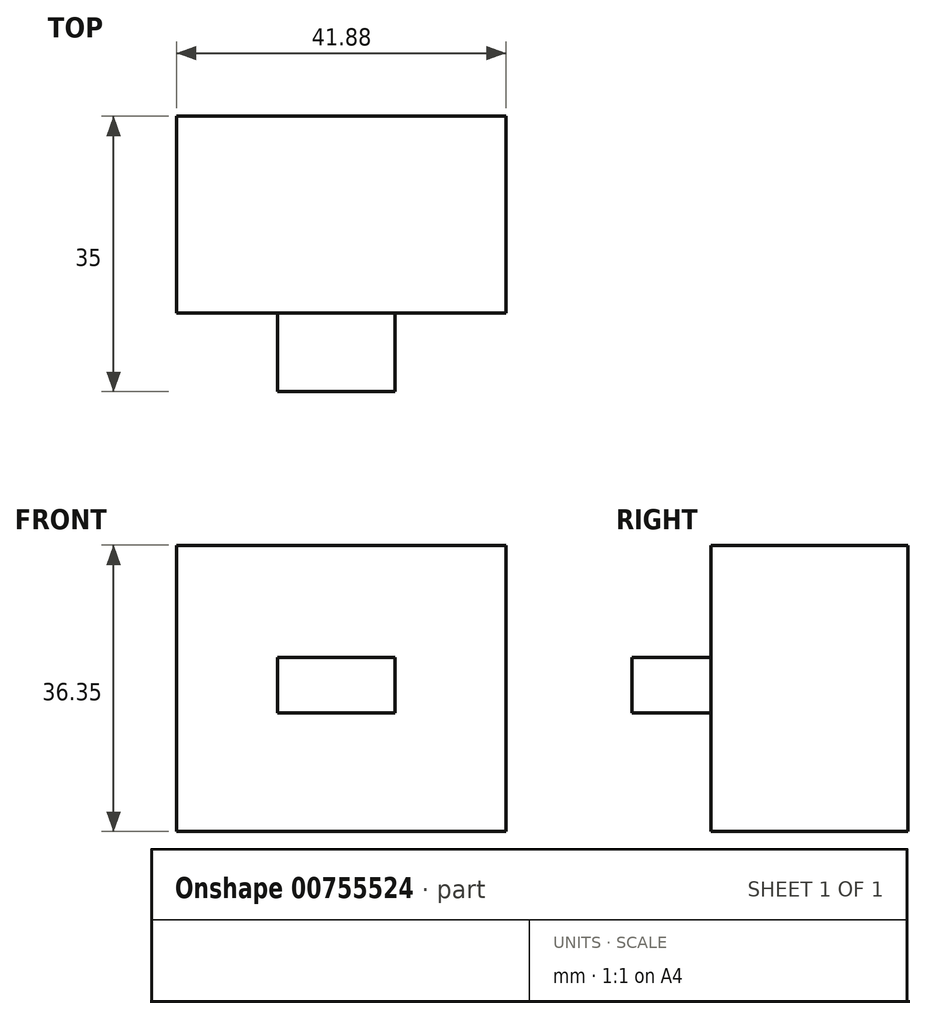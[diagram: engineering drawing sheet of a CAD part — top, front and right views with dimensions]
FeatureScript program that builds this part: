
annotation { "Feature Type Name" : "Feature", "Feature Type Description" : "" }
export const myFeature = defineFeature(function(context is Context, id is Id, definition is map)
    precondition{}
    {
        {
            var Q0;
            Q0=qCreatedBy(makeId("Front.planeOp"),FACE);
            var sketch = newSketch(context, id + "F0", { "sketchPlane" : qUnion([Q0])});
            skLineSegment(sketch, "E0.bottom", {"start": v(-45.5, 40.8) * mm, "end": v(-3.63, 40.8) * mm});
            skLineSegment(sketch, "E0.top", {"start": v(-45.5, 4.45) * mm, "end": v(-3.63, 4.45) * mm});
            skLineSegment(sketch, "E0.left", {"start": v(-45.5, 40.8) * mm, "end": v(-45.5, 4.45) * mm});
            skLineSegment(sketch, "E0.right", {"start": v(-3.63, 40.8) * mm, "end": v(-3.63, 4.45) * mm});
            skLineSegment(sketch, "E1.bottom", {"start": v(-32.65, 26.53) * mm, "end": v(-17.76, 26.53) * mm});
            skLineSegment(sketch, "E1.top", {"start": v(-32.65, 19.5) * mm, "end": v(-17.76, 19.5) * mm});
            skLineSegment(sketch, "E1.left", {"start": v(-32.65, 26.53) * mm, "end": v(-32.65, 19.5) * mm});
            skLineSegment(sketch, "E1.right", {"start": v(-17.76, 26.53) * mm, "end": v(-17.76, 19.5) * mm});
            skSolve(sketch);
        }
        {
            var Q0;
            Q0=makeQuery(id+"F0.imprint","IMPRINT",FACE,{"disambiguationData":[TD([[makeQuery(id+"F0.imprint","IMPRINT",EDGE,{"derivedFrom":sQuery(id+"F0.wireOp",EDGE,"E0.bottom")}),-1.0]])]});
            extrude(context, id + "F1", {"entities" : qUnion([Q0]), "depth" : 25 * mm, "offsetDistance" : 25 * mm});
        }
        {
            var Q0;
            Q0=makeQuery(id+"F0.imprint","IMPRINT",FACE,{"disambiguationData":[TD([[makeQuery(id+"F0.imprint","IMPRINT",EDGE,{"derivedFrom":sQuery(id+"F0.wireOp",EDGE,"E1.bottom")}),-1.0]])]});
            var Q1;
            Q1=makeQuery(id+"F1.opExtrude","CAP_FACE",FACE,{"disambiguationData":[OSD([sQuery(id+"F0.wireOp",EDGE,"E0.bottom"),sQuery(id+"F0.wireOp",EDGE,"E0.top"),sQuery(id+"F0.wireOp",EDGE,"E0.left"),sQuery(id+"F0.wireOp",EDGE,"E0.right"),sQuery(id+"F0.wireOp",EDGE,"E1.bottom"),sQuery(id+"F0.wireOp",EDGE,"E1.top"),sQuery(id+"F0.wireOp",EDGE,"E1.left"),sQuery(id+"F0.wireOp",EDGE,"E1.right")])],"isStart":false});
            extrude(context, id + "F2", {"entities" : qUnion([Q0]), "operationType" : NewBodyOperationType.ADD, "endBound" : BoundingType.UP_TO_SURFACE, "depth" : 25 * mm, "endBoundEntityFace" : qUnion([Q1]), "hasOffset" : true, "offsetDistance" : -10 * mm});
        }
    });
